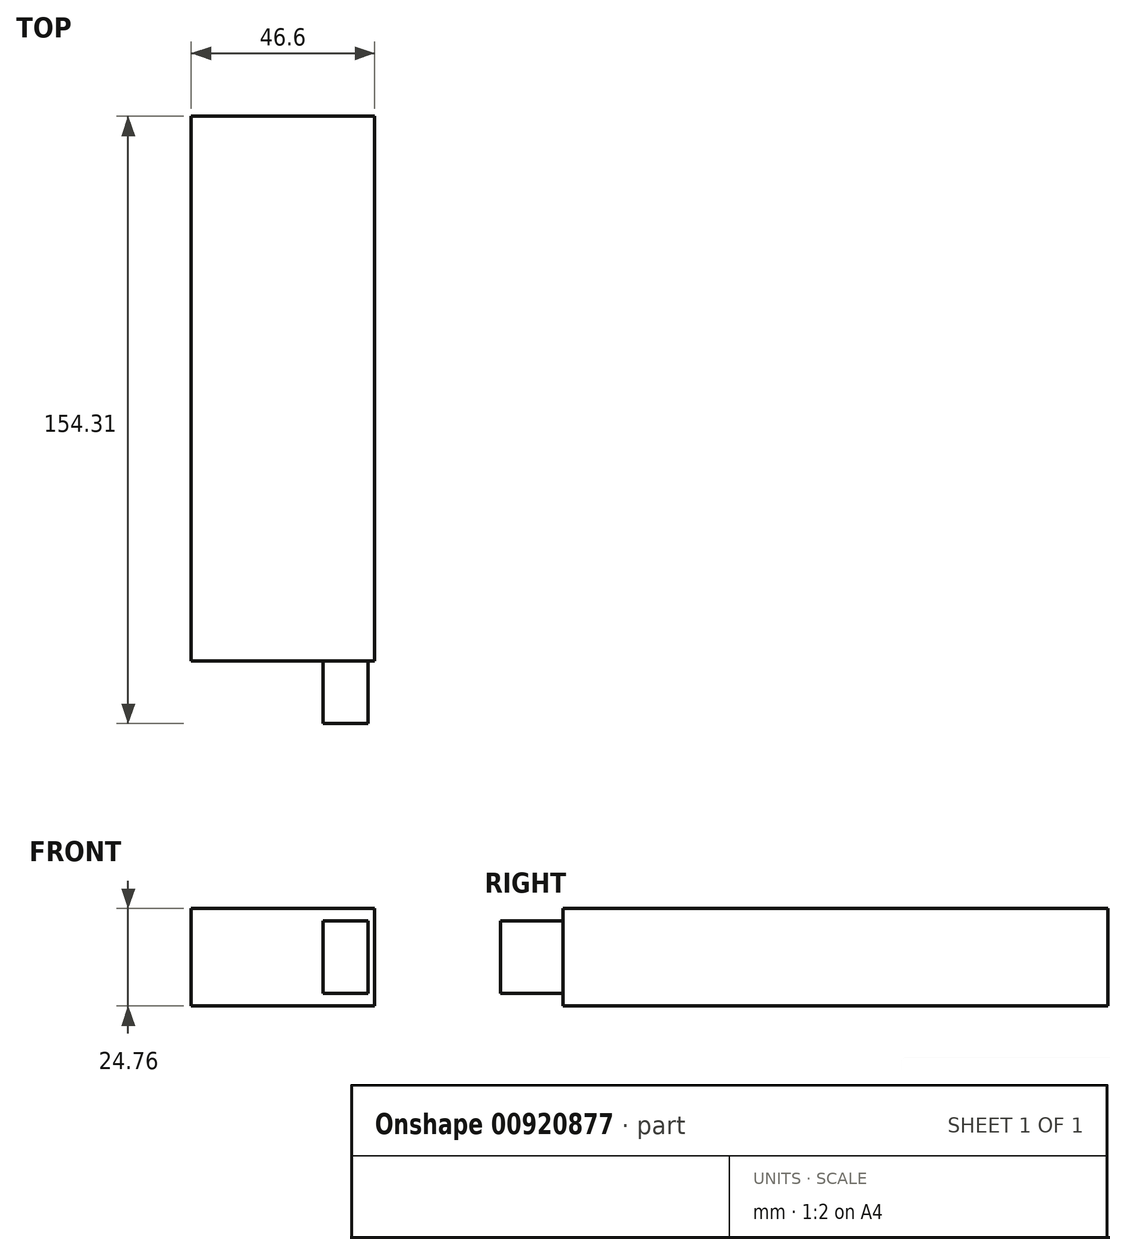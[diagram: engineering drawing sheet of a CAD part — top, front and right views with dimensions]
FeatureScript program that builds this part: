
annotation { "Feature Type Name" : "Feature", "Feature Type Description" : "" }
export const myFeature = defineFeature(function(context is Context, id is Id, definition is map)
    precondition{}
    {
        {
            var Q0;
            Q0=qCreatedBy(makeId("Front.planeOp"),FACE);
            var sketch = newSketch(context, id + "F0", { "sketchPlane" : qUnion([Q0])});
            skLineSegment(sketch, "E0.bottom", {"start": v(23.3, 12.38) * mm, "end": v(-23.3, 12.38) * mm});
            skLineSegment(sketch, "E0.top", {"start": v(23.3, -12.38) * mm, "end": v(-23.3, -12.38) * mm});
            skLineSegment(sketch, "E0.left", {"start": v(23.3, 12.38) * mm, "end": v(23.3, -12.38) * mm});
            skLineSegment(sketch, "E0.right", {"start": v(-23.3, 12.38) * mm, "end": v(-23.3, -12.38) * mm});
            skPoint(sketch, "E0.middle", {"position": v(0, 0) * mm});
            skSolve(sketch);
        }
        {
            var Q0;
            Q0 = qSketchRegion(id + "F0", true);
            extrude(context, id + "F1", {"entities" : qUnion([Q0]), "oppositeDirection" : true, "depth" : 138.43 * mm, "offsetDistance" : 25.4 * mm});
        }
        {
            var Q0;
            Q0=makeQuery(id+"F1.opExtrude","CAP_FACE",FACE,{"disambiguationData":[OSD([sQuery(id+"F0.wireOp",EDGE,"E0.bottom"),sQuery(id+"F0.wireOp",EDGE,"E0.top"),sQuery(id+"F0.wireOp",EDGE,"E0.left"),sQuery(id+"F0.wireOp",EDGE,"E0.right")])],"isStart":true});
            var sketch = newSketch(context, id + "F2", { "sketchPlane" : qUnion([Q0])});
            skLineSegment(sketch, "E1.bottom", {"start": v(21.59, 9.2) * mm, "end": v(10.16, 9.2) * mm});
            skLineSegment(sketch, "E1.top", {"start": v(21.59, -9.2) * mm, "end": v(10.16, -9.2) * mm});
            skLineSegment(sketch, "E1.left", {"start": v(21.59, 9.2) * mm, "end": v(21.59, -9.2) * mm});
            skLineSegment(sketch, "E1.right", {"start": v(10.16, 9.2) * mm, "end": v(10.16, -9.2) * mm});
            skPoint(sketch, "E1.middle", {"position": v(15.88, 0) * mm});
            skSolve(sketch);
        }
        {
            var Q0;
            Q0 = qSketchRegion(id + "F2", true);
            extrude(context, id + "F3", {"entities" : qUnion([Q0]), "operationType" : NewBodyOperationType.ADD, "depth" : 15.88 * mm, "offsetDistance" : 25.4 * mm});
        }
    });
